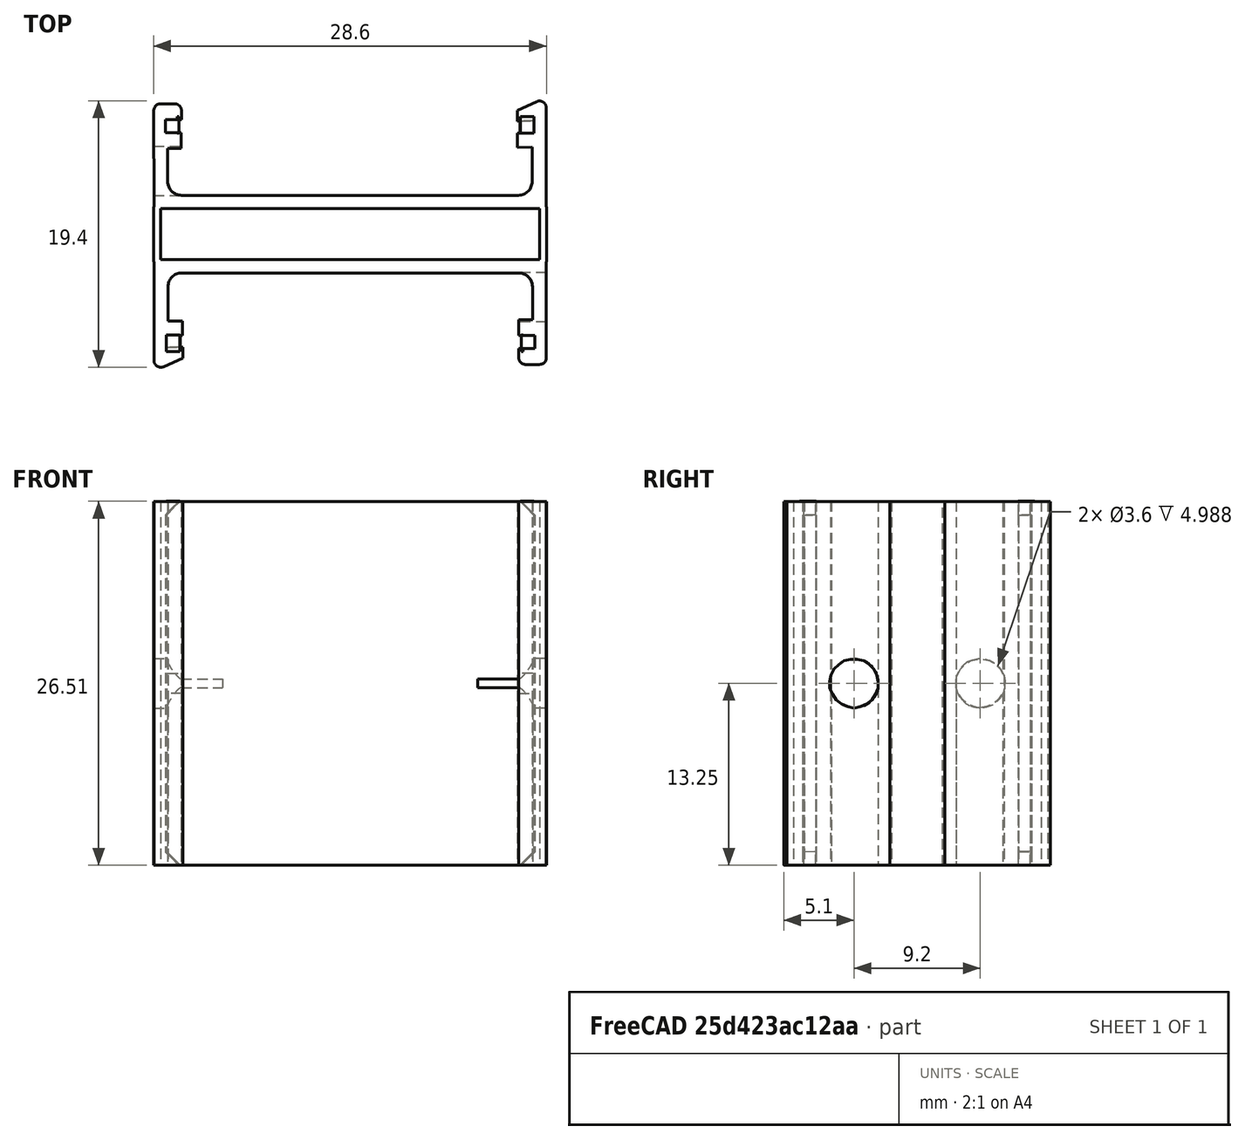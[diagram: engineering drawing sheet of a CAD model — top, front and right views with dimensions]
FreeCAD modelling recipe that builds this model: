
FCSTD DOCUMENT  (FreeCAD 0.18.4R)
Label: GPSAntennaClip3
License: All rights reserved
LicenseURL: http://en.wikipedia.org/wiki/All_rights_reserved
objects: Sketcher::SketchObject×10, PartDesign::Pad×10, Part::Fillet×4, Part::MultiFuse×3, Part::Cylinder×2, Part::Box×2, Part::Cut×2, Mesh::Feature×1
note: 43 computed .brp shape members not serialized (recipe doc carries the construction recipe); baked Part::Feature solids carry a one-line shape summary decoded from their .brp

FEATURE [Sketcher::SketchObject] Sketch
  MapMode = 5
  Placement = pos=(-13.6,0,29.03) rot=(0,1,0;1.5708rad)
  sketch-geometry (20):
    g0: LineSegment StartX=-11.5249 StartY=-10.672 StartZ=0 EndX=15.0066 EndY=-10.672 EndZ=0
    g1: LineSegment StartX=16.0148 StartY=-11.6524 StartZ=0 EndX=-12.5379 EndY=-11.6524 EndZ=0
    g2: LineSegment StartX=16.0192 StartY=-4.00811 StartZ=0 EndX=16.0148 EndY=-11.6524 EndZ=0
    g3: LineSegment StartX=14.0057 StartY=-4.0048 StartZ=0 EndX=14.0074 EndY=-5.15776 EndZ=0
    g4: LineSegment StartX=14.0057 StartY=-4.0048 StartZ=0 EndX=16.0192 EndY=-4.00811 EndZ=0
    g5: LineSegment StartX=14.0074 StartY=-5.15776 StartZ=0 EndX=15.1715 EndY=-5.15776 EndZ=0
    g6: LineSegment StartX=15.1715 StartY=-5.15776 StartZ=0 EndX=15.1785 EndY=-6.1172 EndZ=0
    g7: LineSegment StartX=15.1785 StartY=-6.1172 StartZ=0 EndX=14.0167 EndY=-6.11499 EndZ=0
    g8: LineSegment StartX=14.0167 StartY=-6.11499 StartZ=0 EndX=14.0167 EndY=-7.25961 EndZ=0
    g9: LineSegment StartX=-10.4599 StartY=-6.13197 StartZ=0 EndX=-11.6397 EndY=-6.14295 EndZ=0
    g10: LineSegment StartX=-11.6397 StartY=-6.14295 StartZ=0 EndX=-11.6339 EndY=-5.26902 EndZ=0
    g11: LineSegment StartX=-11.6339 StartY=-5.26902 StartZ=0 EndX=-10.4434 EndY=-5.27468 EndZ=0
    g12: LineSegment StartX=-10.4434 StartY=-5.27468 StartZ=0 EndX=-10.453 EndY=-4.4836 EndZ=0
    g13: LineSegment StartX=-10.453 StartY=-4.4836 StartZ=0 EndX=-12.5475 EndY=-3.52212 EndZ=0
    g14: LineSegment StartX=-12.5475 StartY=-3.52212 StartZ=0 EndX=-12.5379 EndY=-11.6524 EndZ=0
    g15: LineSegment StartX=14.0167 StartY=-7.25961 StartZ=0 EndX=15.0074 EndY=-7.25703 EndZ=0
    g16: LineSegment StartX=15.0074 StartY=-7.25703 StartZ=0 EndX=15.0066 EndY=-10.672 EndZ=0
    g17: LineSegment StartX=-10.4599 StartY=-6.13197 StartZ=0 EndX=-10.4599 EndY=-7.18354 EndZ=0
    g18: LineSegment StartX=-10.4599 StartY=-7.18354 StartZ=0 EndX=-11.5249 EndY=-7.1747 EndZ=0
    g19: LineSegment StartX=-11.5249 StartY=-7.1747 StartZ=0 EndX=-11.5249 EndY=-10.672 EndZ=0
  constraints (21):
    c: Horizontal(g1)
    c: Coincident(g1,g2)
    c: Coincident(g4,g3)
    c: Coincident(g3,g5)
    c: Coincident(g5,g6)
    c: Coincident(g6,g7)
    c: Coincident(g8,g7)
    c: Coincident(g4,g2)
    c: Coincident(g9,g10)
    c: Coincident(g10,g11)
    c: Coincident(g11,g12)
    c: Coincident(g12,g13)
    c: Coincident(g14,g13)
    c: Coincident(g14,g1)
    c: Coincident(g15,g8)
    c: Coincident(g15,g16)
    c: Coincident(g16,g0)
    c: Coincident(g9,g17)
    c: Coincident(g17,g18)
    c: Coincident(g18,g19)
    c: Coincident(g0,g19)
FEATURE [PartDesign::Pad] Pad
  Length = 26.5
  Length2 = 100
  Placement = pos=(-13.6,0,29.03) rot=(0,1,0;1.5708rad)
  Profile = -> Sketch
  Type = 0
FEATURE [Sketcher::SketchObject] Sketch004
  MapMode = 5
  Placement = pos=(-6.6,-4.95,19.85) rot=(1,0,0;1.5708rad)
  sketch-geometry (3):
    g0: LineSegment StartX=-7.00166 StartY=-5.01077 StartZ=0 EndX=-6.98953 EndY=-6.02972 EndZ=0
    g1: LineSegment StartX=-6.98953 StartY=-6.02972 StartZ=0 EndX=-5.96627 EndY=-6.02972 EndZ=0
    g2: LineSegment StartX=-7.00166 StartY=-5.01077 StartZ=0 EndX=-5.96627 EndY=-6.02972 EndZ=0
  constraints (3):
    c: Coincident(g0,g1)
    c: Coincident(g2,g0)
    c: Coincident(g2,g1)
FEATURE [PartDesign::Pad] Pad004  label="stopper002"
  Length = 1.2
  Length2 = 100
  Placement = pos=(-6.6,-4.95,19.85) rot=(1,0,0;1.5708rad)
  Profile = -> Sketch004
  Type = 0
FEATURE [Sketcher::SketchObject] Sketch006
  MapMode = 5
  Placement = pos=(12.9,-4.95,13.85) rot=(1,0,0;1.5708rad)
  sketch-geometry (3):
    g0: LineSegment StartX=-0.005347 StartY=0.971544 StartZ=0 EndX=-0.005347 EndY=-0.027131 EndZ=0
    g1: LineSegment StartX=-0.005347 StartY=-0.027131 StartZ=0 EndX=-1.00402 EndY=-0.027124 EndZ=0
    g2: LineSegment StartX=-1.00402 StartY=-0.027124 StartZ=0 EndX=-0.005347 EndY=0.971544 EndZ=0
  constraints (3):
    c: Coincident(g0,g1)
    c: Coincident(g1,g2)
    c: Coincident(g2,g0)
FEATURE [PartDesign::Pad] Pad006  label="stopper003"
  Length = 1.2
  Length2 = 100
  Placement = pos=(12.9,-4.95,13.85) rot=(1,0,0;1.5708rad)
  Profile = -> Sketch006
  Type = 0
FEATURE [Sketcher::SketchObject] Sketch007
  MapMode = 5
  Placement = pos=(12.9,-4.95,39.7) rot=(1,0,0;1.5708rad)
  sketch-geometry (3):
    g0: LineSegment StartX=-0.005347 StartY=0.971544 StartZ=0 EndX=-0.005347 EndY=-0.027131 EndZ=0
    g1: LineSegment StartX=-0.005347 StartY=-0.027131 StartZ=0 EndX=-1.00779 EndY=0.969763 EndZ=0
    g2: LineSegment StartX=-1.00779 StartY=0.969763 StartZ=0 EndX=-0.005347 EndY=0.971544 EndZ=0
  constraints (3):
    c: Coincident(g0,g1)
    c: Coincident(g1,g2)
    c: Coincident(g2,g0)
FEATURE [PartDesign::Pad] Pad007  label="stopper004"
  Length = 1.2
  Length2 = 100
  Placement = pos=(12.9,-4.95,39.7) rot=(1,0,0;1.5708rad)
  Profile = -> Sketch007
  Type = 0
FEATURE [Sketcher::SketchObject] Sketch008
  MapMode = 5
  Placement = pos=(-12.6,-4.95,39.7) rot=(1,0,0;1.5708rad)
  sketch-geometry (3):
    g0: LineSegment StartX=-0.005347 StartY=0.971544 StartZ=0 EndX=-1.00207 EndY=-0.002707 EndZ=0
    g1: LineSegment StartX=-1.00207 StartY=-0.002707 StartZ=0 EndX=-1.00779 EndY=0.969763 EndZ=0
    g2: LineSegment StartX=-1.00779 StartY=0.969763 StartZ=0 EndX=-0.005347 EndY=0.971544 EndZ=0
  constraints (3):
    c: Coincident(g0,g1)
    c: Coincident(g1,g2)
    c: Coincident(g2,g0)
FEATURE [PartDesign::Pad] Pad008  label="stopper001"
  Length = 1.2
  Length2 = 100
  Placement = pos=(-12.6,-4.95,39.7) rot=(1,0,0;1.5708rad)
  Profile = -> Sketch008
  Type = 0
FEATURE [Part::Cylinder] Cylinder  label="Zylinder"
  Angle = 360
  AttacherType = Attacher::AttachEngine3D
  Height = 10
  Placement = pos=(-0.35,-8.9,8) rot=(0,0,1;0rad)
  Radius = 1.8
FEATURE [Part::Box] Box  label="Würfel002"
  AttacherType = Attacher::AttachEngine3D
  Height = 26.5
  Length = 0.5
  Placement = pos=(41.1,-15.5,-12.9) rot=(0,0,1;0rad)
  Width = 4
FEATURE [Part::Box] Box001  label="Würfel001"
  AttacherType = Attacher::AttachEngine3D
  Height = 26.5
  Length = 0.5
  Placement = pos=(13,-15.5,-12.9) rot=(0,0,1;0rad)
  Width = 4
FEATURE [Part::MultiFuse] Fusion
  Shapes = -> [Pad,Pad004,Pad006,Pad007,Pad008]
FEATURE [Part::Cut] Cut
  Base = -> Fusion
  Placement = pos=(0,0,0) rot=(0,1,0;1.5708rad)
  Tool = -> Cylinder
FEATURE [Part::Fillet] Fillet
  Base = -> Cut
  Edges = 3 edges r=1: [Edge73,Edge115,Edge120]
FEATURE [Part::Fillet] Fillet001
  Base = -> Fillet
  Edges = 3 edges r=0.5: [Edge108,Edge110,Edge112]
FEATURE [Sketcher::SketchObject] Sketch009
  MapMode = 5
  Placement = pos=(-13.6,0,29.03) rot=(0,1,0;1.5708rad)
  sketch-geometry (20):
    g0: LineSegment StartX=-11.5249 StartY=-10.672 StartZ=0 EndX=15.0066 EndY=-10.672 EndZ=0
    g1: LineSegment StartX=16.0148 StartY=-11.6524 StartZ=0 EndX=-12.5379 EndY=-11.6524 EndZ=0
    g2: LineSegment StartX=16.0192 StartY=-4.00811 StartZ=0 EndX=16.0148 EndY=-11.6524 EndZ=0
    g3: LineSegment StartX=14.0057 StartY=-4.0048 StartZ=0 EndX=14.0074 EndY=-5.15776 EndZ=0
    g4: LineSegment StartX=14.0057 StartY=-4.0048 StartZ=0 EndX=16.0192 EndY=-4.00811 EndZ=0
    g5: LineSegment StartX=14.0074 StartY=-5.15776 StartZ=0 EndX=15.1715 EndY=-5.15776 EndZ=0
    g6: LineSegment StartX=15.1715 StartY=-5.15776 StartZ=0 EndX=15.1785 EndY=-6.1172 EndZ=0
    g7: LineSegment StartX=15.1785 StartY=-6.1172 StartZ=0 EndX=14.0167 EndY=-6.11499 EndZ=0
    g8: LineSegment StartX=14.0167 StartY=-6.11499 StartZ=0 EndX=14.0167 EndY=-7.25961 EndZ=0
    g9: LineSegment StartX=-10.4599 StartY=-6.13197 StartZ=0 EndX=-11.6397 EndY=-6.14295 EndZ=0
    g10: LineSegment StartX=-11.6397 StartY=-6.14295 StartZ=0 EndX=-11.6339 EndY=-5.26902 EndZ=0
    g11: LineSegment StartX=-11.6339 StartY=-5.26902 StartZ=0 EndX=-10.4434 EndY=-5.27468 EndZ=0
    g12: LineSegment StartX=-10.4434 StartY=-5.27468 StartZ=0 EndX=-10.453 EndY=-4.4836 EndZ=0
    g13: LineSegment StartX=-10.453 StartY=-4.4836 StartZ=0 EndX=-12.5475 EndY=-3.52212 EndZ=0
    g14: LineSegment StartX=-12.5475 StartY=-3.52212 StartZ=0 EndX=-12.5379 EndY=-11.6524 EndZ=0
    g15: LineSegment StartX=14.0167 StartY=-7.25961 StartZ=0 EndX=15.0074 EndY=-7.25703 EndZ=0
    g16: LineSegment StartX=15.0074 StartY=-7.25703 StartZ=0 EndX=15.0066 EndY=-10.672 EndZ=0
    g17: LineSegment StartX=-10.4599 StartY=-6.13197 StartZ=0 EndX=-10.4599 EndY=-7.18354 EndZ=0
    g18: LineSegment StartX=-10.4599 StartY=-7.18354 StartZ=0 EndX=-11.5249 EndY=-7.1747 EndZ=0
    g19: LineSegment StartX=-11.5249 StartY=-7.1747 StartZ=0 EndX=-11.5249 EndY=-10.672 EndZ=0
  constraints (21):
    c: Horizontal(g1)
    c: Coincident(g1,g2)
    c: Coincident(g4,g3)
    c: Coincident(g3,g5)
    c: Coincident(g5,g6)
    c: Coincident(g6,g7)
    c: Coincident(g8,g7)
    c: Coincident(g4,g2)
    c: Coincident(g9,g10)
    c: Coincident(g10,g11)
    c: Coincident(g11,g12)
    c: Coincident(g12,g13)
    c: Coincident(g14,g13)
    c: Coincident(g14,g1)
    c: Coincident(g15,g8)
    c: Coincident(g15,g16)
    c: Coincident(g16,g0)
    c: Coincident(g9,g17)
    c: Coincident(g17,g18)
    c: Coincident(g18,g19)
    c: Coincident(g0,g19)
FEATURE [PartDesign::Pad] Pad009
  Length = 26.5
  Length2 = 100
  Placement = pos=(-13.6,0,29.03) rot=(0,1,0;1.5708rad)
  Profile = -> Sketch009
  Type = 0
FEATURE [Sketcher::SketchObject] Sketch010
  MapMode = 5
  Placement = pos=(-6.6,-4.95,19.85) rot=(1,0,0;1.5708rad)
  sketch-geometry (3):
    g0: LineSegment StartX=-7.00166 StartY=-5.01077 StartZ=0 EndX=-6.98953 EndY=-6.02972 EndZ=0
    g1: LineSegment StartX=-6.98953 StartY=-6.02972 StartZ=0 EndX=-5.96627 EndY=-6.02972 EndZ=0
    g2: LineSegment StartX=-7.00166 StartY=-5.01077 StartZ=0 EndX=-5.96627 EndY=-6.02972 EndZ=0
  constraints (3):
    c: Coincident(g0,g1)
    c: Coincident(g2,g0)
    c: Coincident(g2,g1)
FEATURE [PartDesign::Pad] Pad010  label="stopper005"
  Length = 1.2
  Length2 = 100
  Placement = pos=(-6.6,-4.95,19.85) rot=(1,0,0;1.5708rad)
  Profile = -> Sketch010
  Type = 0
FEATURE [Sketcher::SketchObject] Sketch011
  MapMode = 5
  Placement = pos=(12.9,-4.95,13.85) rot=(1,0,0;1.5708rad)
  sketch-geometry (3):
    g0: LineSegment StartX=-0.005347 StartY=0.971544 StartZ=0 EndX=-0.005347 EndY=-0.027131 EndZ=0
    g1: LineSegment StartX=-0.005347 StartY=-0.027131 StartZ=0 EndX=-1.00402 EndY=-0.027124 EndZ=0
    g2: LineSegment StartX=-1.00402 StartY=-0.027124 StartZ=0 EndX=-0.005347 EndY=0.971544 EndZ=0
  constraints (3):
    c: Coincident(g0,g1)
    c: Coincident(g1,g2)
    c: Coincident(g2,g0)
FEATURE [PartDesign::Pad] Pad011  label="stopper006"
  Length = 1.2
  Length2 = 100
  Placement = pos=(12.9,-4.95,13.85) rot=(1,0,0;1.5708rad)
  Profile = -> Sketch011
  Type = 0
FEATURE [Sketcher::SketchObject] Sketch012
  MapMode = 5
  Placement = pos=(12.9,-4.95,39.7) rot=(1,0,0;1.5708rad)
  sketch-geometry (3):
    g0: LineSegment StartX=-0.005347 StartY=0.971544 StartZ=0 EndX=-0.005347 EndY=-0.027131 EndZ=0
    g1: LineSegment StartX=-0.005347 StartY=-0.027131 StartZ=0 EndX=-1.00779 EndY=0.969763 EndZ=0
    g2: LineSegment StartX=-1.00779 StartY=0.969763 StartZ=0 EndX=-0.005347 EndY=0.971544 EndZ=0
  constraints (3):
    c: Coincident(g0,g1)
    c: Coincident(g1,g2)
    c: Coincident(g2,g0)
FEATURE [PartDesign::Pad] Pad012  label="stopper007"
  Length = 1.2
  Length2 = 100
  Placement = pos=(12.9,-4.95,39.7) rot=(1,0,0;1.5708rad)
  Profile = -> Sketch012
  Type = 0
FEATURE [Sketcher::SketchObject] Sketch013
  MapMode = 5
  Placement = pos=(-12.6,-4.95,39.7) rot=(1,0,0;1.5708rad)
  sketch-geometry (3):
    g0: LineSegment StartX=-0.005347 StartY=0.971544 StartZ=0 EndX=-1.00207 EndY=-0.002707 EndZ=0
    g1: LineSegment StartX=-1.00207 StartY=-0.002707 StartZ=0 EndX=-1.00779 EndY=0.969763 EndZ=0
    g2: LineSegment StartX=-1.00779 StartY=0.969763 StartZ=0 EndX=-0.005347 EndY=0.971544 EndZ=0
  constraints (3):
    c: Coincident(g0,g1)
    c: Coincident(g1,g2)
    c: Coincident(g2,g0)
FEATURE [PartDesign::Pad] Pad013  label="stopper008"
  Length = 1.2
  Length2 = 100
  Placement = pos=(-12.6,-4.95,39.7) rot=(1,0,0;1.5708rad)
  Profile = -> Sketch013
  Type = 0
FEATURE [Part::Cylinder] Cylinder001  label="Zylinder001"
  Angle = 360
  AttacherType = Attacher::AttachEngine3D
  Height = 10
  Placement = pos=(-0.35,-8.9,8) rot=(0,0,1;0rad)
  Radius = 1.8
FEATURE [Part::MultiFuse] Fusion001
  Shapes = -> [Pad009,Pad010,Pad011,Pad012,Pad013]
FEATURE [Part::Cut] Cut001
  Base = -> Fusion001
  Placement = pos=(0,0,0) rot=(0,1,0;1.5708rad)
  Tool = -> Cylinder001
FEATURE [Part::Fillet] Fillet002
  Base = -> Cut001
  Edges = 3 edges r=1: [Edge73,Edge115,Edge120]
FEATURE [Part::Fillet] Fillet003
  Base = -> Fillet002
  Edges = 3 edges r=0.5: [Edge108,Edge110,Edge112]
  Placement = pos=(54.6,-27,0) rot=(0,0,1;3.14159rad)
FEATURE [Part::MultiFuse] Fusion002
  Shapes = -> [Fillet003,Fillet001,Box,Box001]
FEATURE [Mesh::Feature] Mesh  label="Fusion002 (Meshed)"
